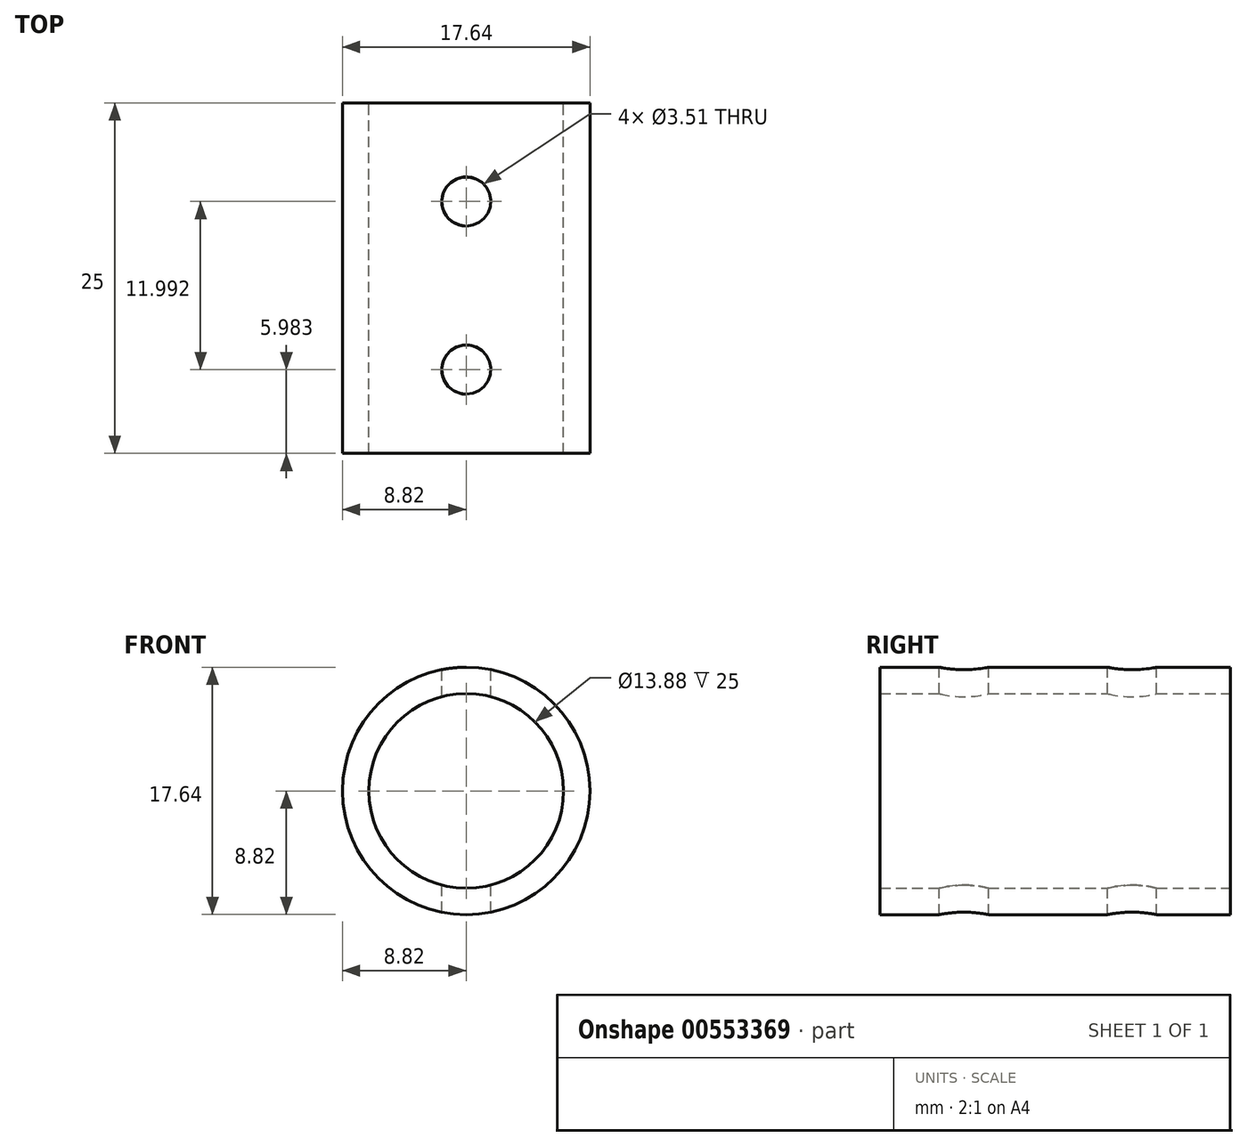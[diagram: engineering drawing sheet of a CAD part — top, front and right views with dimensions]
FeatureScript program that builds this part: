
annotation { "Feature Type Name" : "Feature", "Feature Type Description" : "" }
export const myFeature = defineFeature(function(context is Context, id is Id, definition is map)
    precondition{}
    {
        {
            var Q0;
            Q0=qCreatedBy(makeId("Front.planeOp"),FACE);
            var sketch = newSketch(context, id + "F0", { "sketchPlane" : qUnion([Q0])});
            skCircle(sketch, "E0", {"center": v(0, -8.7) * mm, "radius": 6.94 * mm});
            skCircle(sketch, "E1", {"center": v(0, -8.7) * mm, "radius": 8.82 * mm});
            skSolve(sketch);
        }
        {
            var Q0;
            Q0 = qSketchRegion(id + "F0", true);
            extrude(context, id + "F1", {"entities" : qUnion([Q0]), "depth" : 25 * mm, "offsetDistance" : 25 * mm});
        }
        {
            var Q0;
            Q0=qCreatedBy(makeId("Top.planeOp"),FACE);
            var sketch = newSketch(context, id + "F2", { "sketchPlane" : qUnion([Q0])});
            skCircle(sketch, "E2", {"center": v(0, -7.02) * mm, "radius": 1.75 * mm});
            skCircle(sketch, "E3", {"center": v(0, -19.02) * mm, "radius": 1.75 * mm});
            skSolve(sketch);
        }
        {
            var Q0;
            Q0=makeQuery(id+"F2.imprint","IMPRINT",FACE,{"disambiguationData":[TD([[makeQuery(id+"F2.imprint","IMPRINT",EDGE,{"derivedFrom":sQuery(id+"F2.wireOp",EDGE,"E2")}),1.0]])]});
            var Q1;
            Q1=makeQuery(id+"F2.imprint","IMPRINT",FACE,{"disambiguationData":[TD([[makeQuery(id+"F2.imprint","IMPRINT",EDGE,{"derivedFrom":sQuery(id+"F2.wireOp",EDGE,"E3")}),1.0]])]});
            extrude(context, id + "F3", {"entities" : qUnion([Q0, Q1]), "operationType" : NewBodyOperationType.REMOVE, "oppositeDirection" : true, "depth" : 25 * mm, "offsetDistance" : 25 * mm, "hasSecondDirection" : true, "secondDirectionOppositeDirection" : false, "secondDirectionDepth" : 25 * mm});
        }
    });
